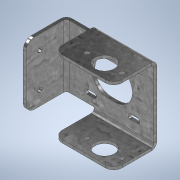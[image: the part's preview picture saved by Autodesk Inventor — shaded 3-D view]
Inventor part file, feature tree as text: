
AUTODESK INVENTOR PART (.ipt)
format: ipt  version: 2022 (Build 260153000, 153)  size: 361,984 bytes
history: native  units: in
note: dims shown in document units (in); Inventor stores cm internally (conversion verified against a paired STEP export)
features: sheet_metal_op x7, other x5, sketch x4, hole x2, chamfer x1
ambient origin geometry x8: Origin, YZ Plane, XZ Plane, XY Plane, X Axis, Y Axis, Z Axis, Center Point
bodies: Solid2 (feature_tree)
feature tree (19):
  sheet_metal_op  "Face1"
  sheet_metal_op  "Flange2"
  sketch  "Sketch3"  dims[d1=2.1654in d4=1.2205in]
  hole  "Hole2"  [1 undecoded]
  sheet_metal_op  "Flange3"
  chamfer  "Corner Round2"
  hole  "Hole3"  [1 undecoded]
  other  "Plate1"
  sketch  "Sketch6"  dims[d7=1.2205in d8=1.2205in]
  other  "Plate4"
  sheet_metal_op  "Bend3"
  sheet_metal_op  "Corner2"
  sketch  "Sketch7"  dims[d9=1.2205in]
  other  "Plate5"
  sheet_metal_op  "Bend4"
  sheet_metal_op  "Corner3"
  sketch  "Sketch8"  dims[d10=1.2205in d11=0.0669in d12=0.1969in d13=0.4724in d14=0.1969in d15=0.5906in d16=0.08in d36=0.5512in d41=0.08in d42=0.0in d43=0.1339in d44=0.2362in d45=0.2559in d46=0.1181in d47=90.0deg d48=0.315in d49=0.8108in d53=2.4803in d55=0.4921in d56=0.4921in d83=1.6929in d84=0.1969in d85=0.5512in d86=0.08in d87=0.04in d88=0.16in d89=0.08in d90=1.2205in d91=90.0deg d92=0.08in d93=0.32in d94=0.08in d95=0.08in d96=0.3937in d97=0.1575in d98=0.2362in d99=0.08in d100=0.04in d101=0.16in d102=0.08in d103=1.2205in d104=90.0deg d105=0.08in d106=0.32in d107=0.08in d108=0.08in d109=0.3937in d110=0.3937in d111=0.3937in d112=0.1339in d113=0.2362in d114=0.2559in d115=0.1181in d116=0.6181in d117=0.08in d118=0.8108in]
  other  "Cut1"
  other  "Definition1"
note: 2 required parameter values undecoded (feature->parameter linkage not recoverable at this tier; creation-order binding heuristic only, values carry confidence <= 0.55)
